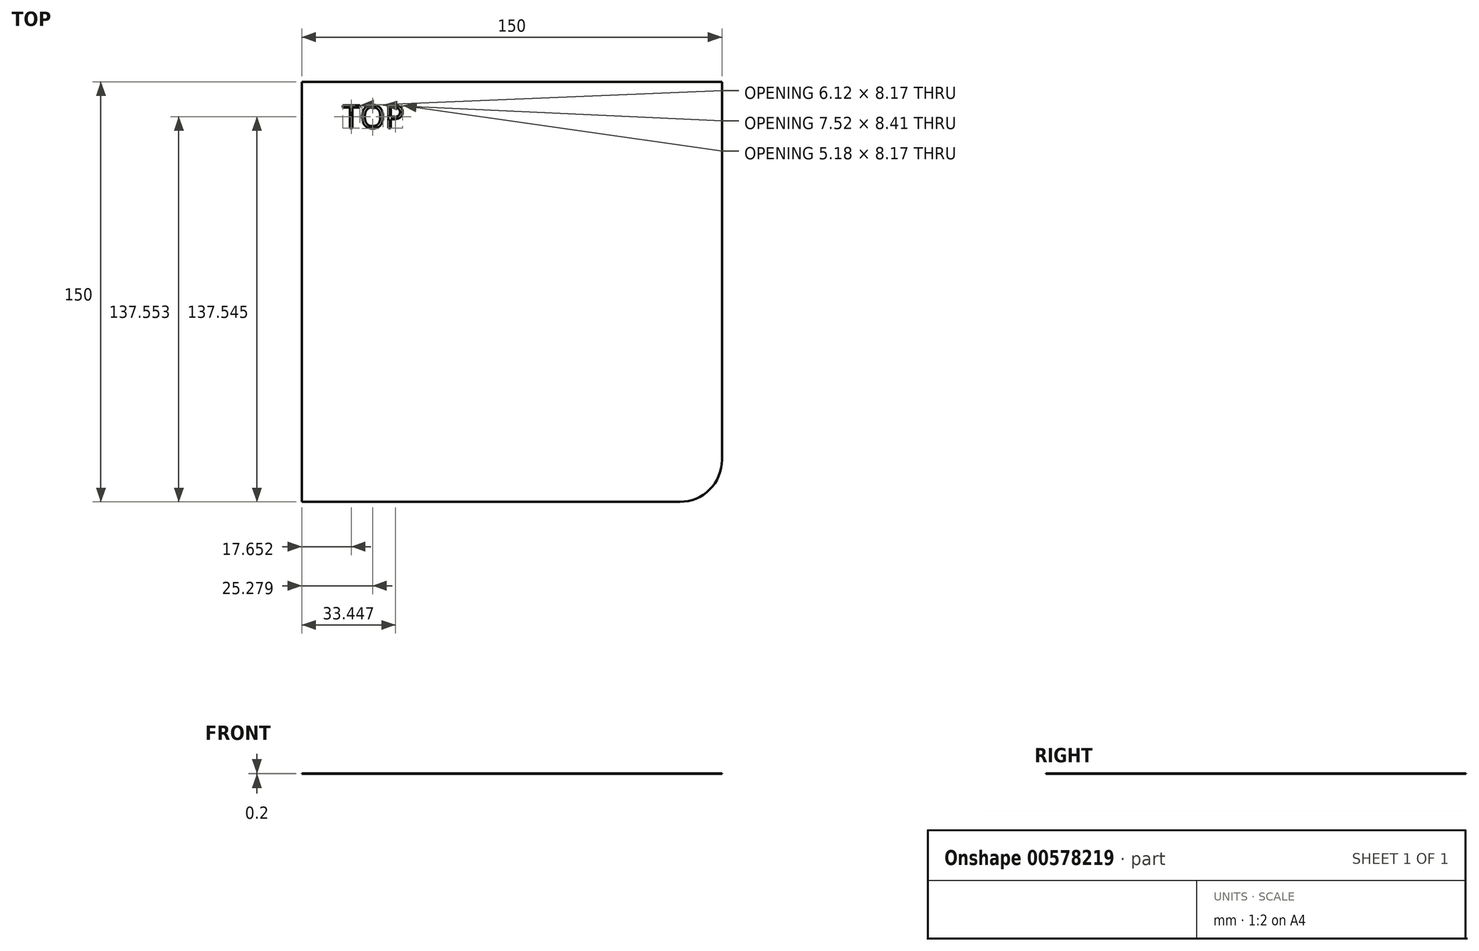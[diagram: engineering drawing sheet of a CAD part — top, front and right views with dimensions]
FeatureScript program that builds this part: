
annotation { "Feature Type Name" : "Feature", "Feature Type Description" : "" }
export const myFeature = defineFeature(function(context is Context, id is Id, definition is map)
    precondition{}
    {
        {
            var Q0;
            Q0=qCreatedBy(makeId("Top.planeOp"),FACE);
            var sketch = newSketch(context, id + "F0", { "sketchPlane" : qUnion([Q0])});
            skLineSegment(sketch, "E0.bottom", {"start": v(0, 0) * mm, "end": v(135, 0) * mm});
            skLineSegment(sketch, "E0.top", {"start": v(0, 150) * mm, "end": v(150, 150) * mm});
            skLineSegment(sketch, "E0.left", {"start": v(0, 0) * mm, "end": v(0, 150) * mm});
            skLineSegment(sketch, "E0.right", {"start": v(150, 15) * mm, "end": v(150, 150) * mm});
            skPoint(sketch, "E1.visualSharp", {"position": v(150, 0) * mm});
            skArc(sketch, "E1.filletArc", {"start": v(135, 0) * mm, "mid": v(145.6, 4.4) * mm, "end": v(150, 15) * mm});
            skSolve(sketch);
        }
        {
            var Q0;
            Q0=makeQuery(id+"F0.imprint","IMPRINT",FACE,{"disambiguationData":[TD([[makeQuery(id+"F0.imprint","IMPRINT",EDGE,{"derivedFrom":sQuery(id+"F0.wireOp",EDGE,"E0.bottom")}),1.0]])]});
            extrude(context, id + "F1", {"entities" : qUnion([Q0]), "depth" : 0.2 * mm, "offsetDistance" : 25 * mm});
        }
        {
            var Q0;
            Q0=makeQuery(id+"F0.imprint","IMPRINT",FACE,{"disambiguationData":[TD([[makeQuery(id+"F0.imprint","IMPRINT",EDGE,{"derivedFrom":sQuery(id+"F0.wireOp",EDGE,"E0.bottom")}),1.0]])]});
            var sketch = newSketch(context, id + "F2", { "sketchPlane" : qUnion([Q0])});
            skText(sketch, "E2", { "text": "TOP", "fontName": "OpenSans-Regular.ttf"});
            const initialGuessF2  = {"E2": [0.01449, 0.13346, 1, 0, 0.00824]};
            skSetInitialGuess(sketch, initialGuessF2);
            skSolve(sketch);
        }
        {
            var Q0;
            Q0 = qSketchRegion(id + "F2", true);
            extrude(context, id + "F3", {"entities" : qUnion([Q0]), "operationType" : NewBodyOperationType.REMOVE, "depth" : 25 * mm, "offsetDistance" : 25 * mm});
        }
    });
